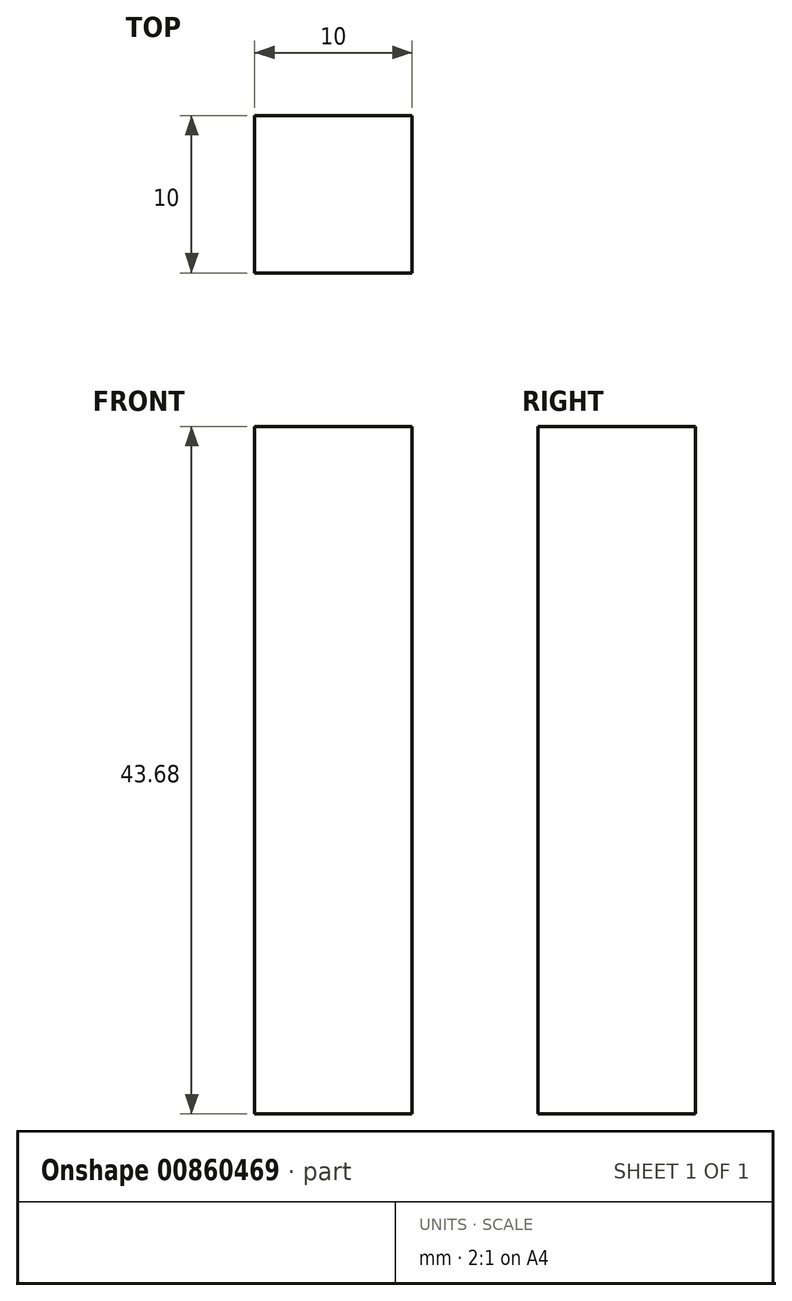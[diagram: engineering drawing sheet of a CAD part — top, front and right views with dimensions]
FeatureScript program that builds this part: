
annotation { "Feature Type Name" : "Feature", "Feature Type Description" : "" }
export const myFeature = defineFeature(function(context is Context, id is Id, definition is map)
    precondition{}
    {
        {
            var Q0;
            Q0=qCreatedBy(makeId("Front.planeOp"),FACE);
            var sketch = newSketch(context, id + "F0", { "sketchPlane" : qUnion([Q0])});
            skLineSegment(sketch, "E0.bottom", {"start": v(1.36, 0) * mm, "end": v(11.36, 0) * mm});
            skLineSegment(sketch, "E0.top", {"start": v(1.36, 43.68) * mm, "end": v(11.36, 43.68) * mm});
            skLineSegment(sketch, "E0.left", {"start": v(1.36, 0) * mm, "end": v(1.36, 43.68) * mm});
            skLineSegment(sketch, "E0.right", {"start": v(11.36, 0) * mm, "end": v(11.36, 43.68) * mm});
            skSolve(sketch);
        }
        {
            var Q0;
            Q0=makeQuery(id+"F0.imprint","IMPRINT",FACE,{"disambiguationData":[TD([[makeQuery(id+"F0.imprint","IMPRINT",EDGE,{"derivedFrom":sQuery(id+"F0.wireOp",EDGE,"E0.bottom")}),1.0]])]});
            extrude(context, id + "F1", {"entities" : qUnion([Q0]), "depth" : 10 * mm, "offsetDistance" : 25 * mm});
        }
    });
